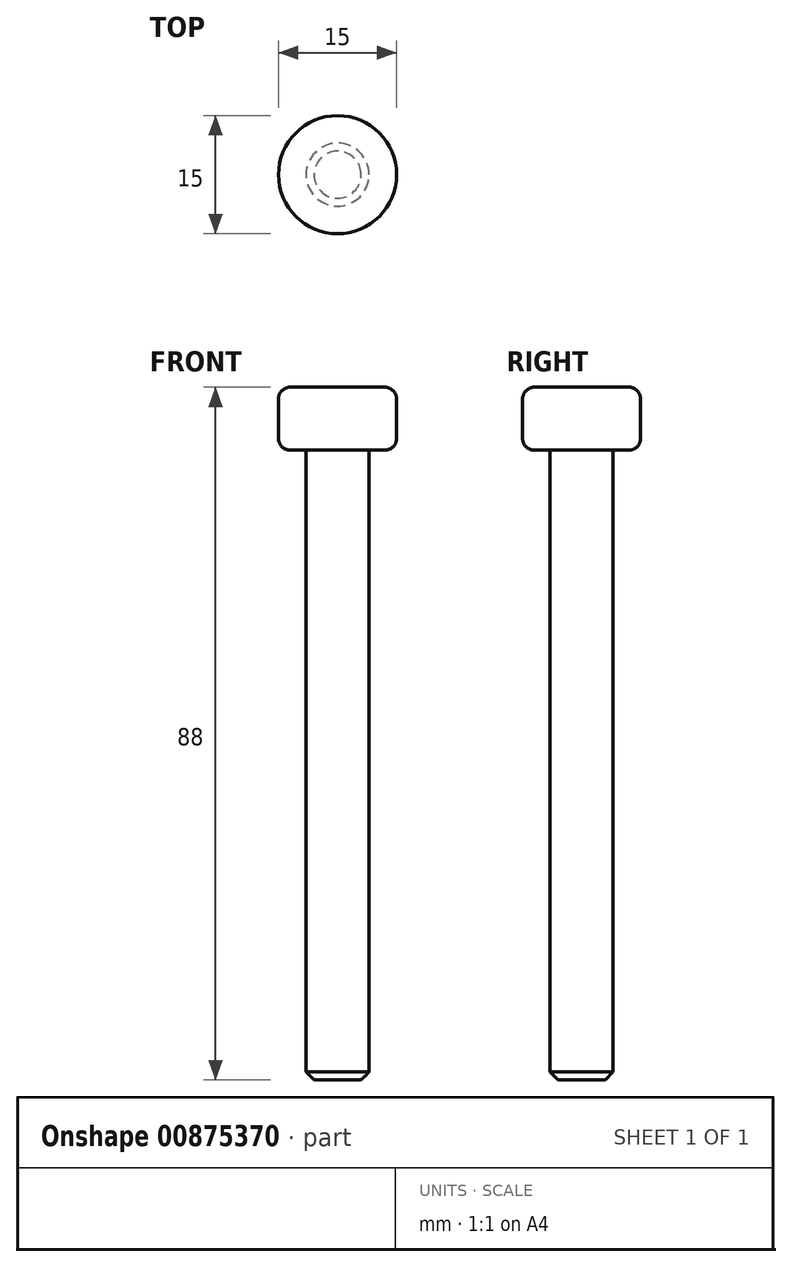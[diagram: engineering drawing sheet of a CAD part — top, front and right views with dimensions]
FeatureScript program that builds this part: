
annotation { "Feature Type Name" : "Feature", "Feature Type Description" : "" }
export const myFeature = defineFeature(function(context is Context, id is Id, definition is map)
    precondition{}
    {
        {
            var Q0;
            Q0=qCreatedBy(makeId("Front.planeOp"),FACE);
            var sketch = newSketch(context, id + "F0", { "sketchPlane" : qUnion([Q0])});
            skLineSegment(sketch, "E0", {"start": v(0, 0) * mm, "end": v(3, 0) * mm});
            skLineSegment(sketch, "E1", {"start": v(3, 0) * mm, "end": v(4, 1) * mm});
            skLineSegment(sketch, "E2", {"start": v(4, 1) * mm, "end": v(4, 80) * mm});
            skLineSegment(sketch, "E3", {"start": v(4, 80) * mm, "end": v(6, 80) * mm});
            skLineSegment(sketch, "E4", {"start": v(7.5, 81.5) * mm, "end": v(7.5, 86.5) * mm});
            skLineSegment(sketch, "E5", {"start": v(6, 88) * mm, "end": v(0, 88) * mm});
            skLineSegment(sketch, "E6", {"start": v(0, 88) * mm, "end": v(0, 0) * mm});
            skPoint(sketch, "E7.visualSharp", {"position": v(7.5, 88) * mm});
            skArc(sketch, "E7.filletArc", {"start": v(7.5, 86.5) * mm, "mid": v(7.06, 87.56) * mm, "end": v(6, 88) * mm});
            skPoint(sketch, "E8.visualSharp", {"position": v(7.5, 80) * mm});
            skArc(sketch, "E8.filletArc", {"start": v(6, 80) * mm, "mid": v(7.06, 80.44) * mm, "end": v(7.5, 81.5) * mm});
            skSolve(sketch);
        }
        {
            var Q0;
            Q0=makeQuery(id+"F0.imprint","IMPRINT",FACE,{"disambiguationData":[TD([[makeQuery(id+"F0.imprint","IMPRINT",EDGE,{"derivedFrom":sQuery(id+"F0.wireOp",EDGE,"E0")}),1.0]])]});
            var Q1;
            Q1=sQuery(id+"F0.wireOp",EDGE,"E6");
            revolve(context, id + "F1", {"surfaceOperationType" : NewSurfaceOperationType.NEW, "entities" : qUnion([Q0]), "axis" : qUnion([Q1]), "revolveType" : RevolveType.FULL});
        }
    });
